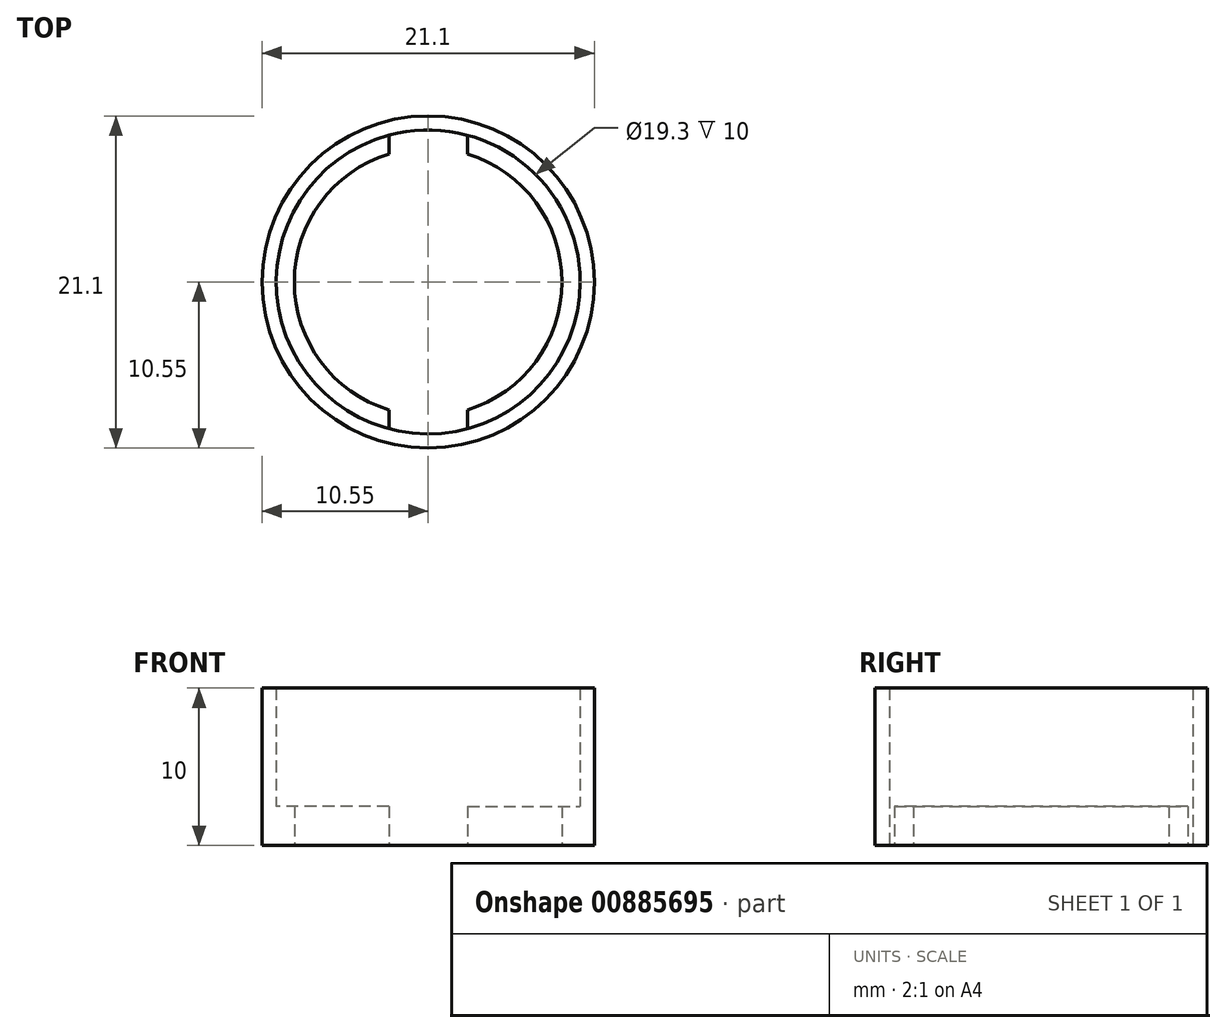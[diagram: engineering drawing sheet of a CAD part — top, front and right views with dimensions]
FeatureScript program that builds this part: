
annotation { "Feature Type Name" : "Feature", "Feature Type Description" : "" }
export const myFeature = defineFeature(function(context is Context, id is Id, definition is map)
    precondition{}
    {
        {
            var Q0;
            Q0=qCreatedBy(makeId("Top.planeOp"),FACE);
            var sketch = newSketch(context, id + "F0", { "sketchPlane" : qUnion([Q0])});
            skCircle(sketch, "E0", {"center": v(0, 0) * mm, "radius": 10.55 * mm});
            skCircle(sketch, "E1", {"center": v(0, 0) * mm, "radius": 9.65 * mm});
            skSolve(sketch);
        }
        {
            var Q0;
            Q0 = qSketchRegion(id + "F0", true);
            extrude(context, id + "F1", {"entities" : qUnion([Q0]), "depth" : 10 * mm, "offsetDistance" : 25 * mm});
        }
        {
            var Q0;
            Q0=makeQuery(id+"F1.opExtrude","CAP_FACE",FACE,{"disambiguationData":[OSD([sQuery(id+"F0.wireOp",EDGE,"E0"),sQuery(id+"F0.wireOp",EDGE,"E1")])],"isStart":true});
            var sketch = newSketch(context, id + "F2", { "sketchPlane" : qUnion([Q0])});
            skArc(sketch, "E2", {"start": v(-2.5, 8.12) * mm, "mid": v(-8.5, 0) * mm, "end": v(-2.5, -8.12) * mm});
            skLineSegment(sketch, "E3.left", {"start": v(-2.5, 9.32) * mm, "end": v(-2.5, 8.12) * mm});
            skLineSegment(sketch, "E3.right", {"start": v(2.5, 9.32) * mm, "end": v(2.5, 8.12) * mm});
            skLineSegment(sketch, "E4.trimOffspring", {"start": v(-2.5, -8.12) * mm, "end": v(-2.5, -9.32) * mm});
            skLineSegment(sketch, "E5.trimOffspring", {"start": v(2.5, -8.12) * mm, "end": v(2.5, -9.32) * mm});
            skArc(sketch, "E6.trimOffspring", {"start": v(2.5, -8.12) * mm, "mid": v(8.5, 0) * mm, "end": v(2.5, 8.12) * mm});
            skArc(sketch, "E7.0", {"start": v(-2.5, 9.32) * mm, "mid": v(-9.65, 0) * mm, "end": v(-2.5, -9.32) * mm});
            skArc(sketch, "E8.trimOffspring", {"start": v(2.5, -9.32) * mm, "mid": v(9.65, 0) * mm, "end": v(2.5, 9.32) * mm});
            skSolve(sketch);
        }
        {
            var Q0;
            Q0 = qSketchRegion(id + "F2", true);
            extrude(context, id + "F3", {"entities" : qUnion([Q0]), "operationType" : NewBodyOperationType.ADD, "oppositeDirection" : true, "depth" : 2.5 * mm, "offsetDistance" : 25 * mm});
        }
    });
